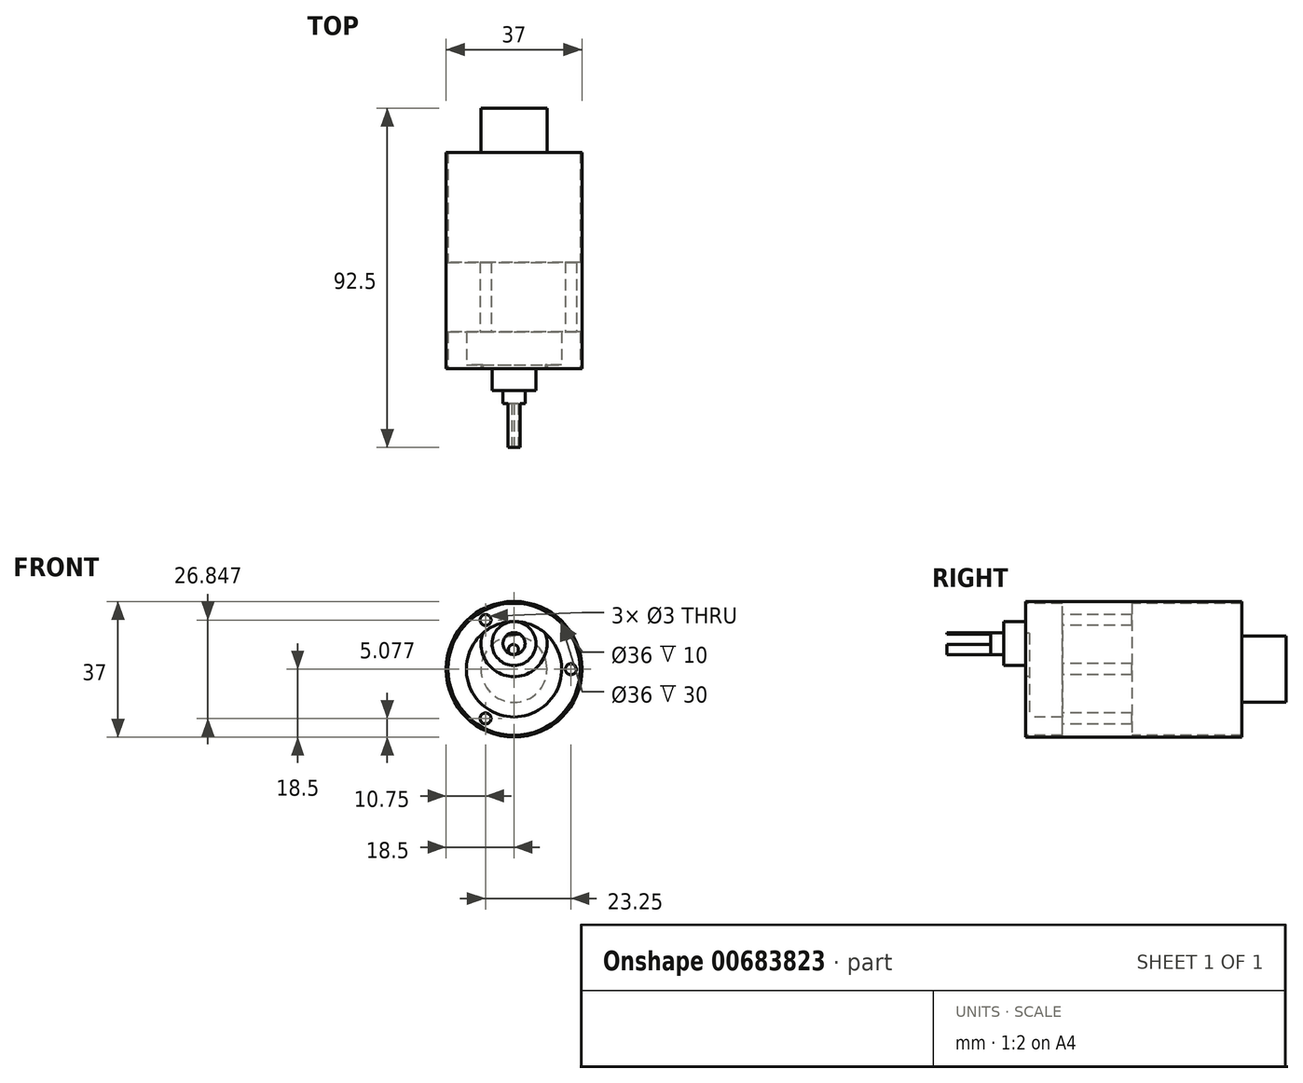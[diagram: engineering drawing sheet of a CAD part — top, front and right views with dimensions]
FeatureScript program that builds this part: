
annotation { "Feature Type Name" : "Feature", "Feature Type Description" : "" }
export const myFeature = defineFeature(function(context is Context, id is Id, definition is map)
    precondition{}
    {
        {
            var Q0;
            Q0=qCreatedBy(makeId("Front.planeOp"),FACE);
            var sketch = newSketch(context, id + "F0", { "sketchPlane" : qUnion([Q0])});
            skCircle(sketch, "E0", {"center": v(0, 0) * mm, "radius": 18.5 * mm});
            skCircle(sketch, "E1", {"center": v(0, 7) * mm, "radius": 6 * mm});
            skCircle(sketch, "E2", {"center": v(0, 0) * mm, "radius": 13 * mm});
            skCircle(sketch, "E3", {"center": v(-15.5, 0) * mm, "radius": 1.5 * mm});
            skCircle(sketch, "E4.MirrorC", {"center": v(15.5, 0) * mm, "radius": 1.5 * mm});
            skCircle(sketch, "E5.1.0", {"center": v(7.75, -13.42) * mm, "radius": 1.5 * mm});
            skCircle(sketch, "E5.1.1", {"center": v(-7.75, 13.42) * mm, "radius": 1.5 * mm});
            skCircle(sketch, "E5.2.0", {"center": v(7.75, 13.42) * mm, "radius": 1.5 * mm});
            skCircle(sketch, "E5.2.1", {"center": v(-7.75, -13.42) * mm, "radius": 1.5 * mm});
            skCircle(sketch, "E6", {"center": v(0, 7) * mm, "radius": 3 * mm});
            skCircle(sketch, "E7", {"center": v(0, 0) * mm, "radius": 18 * mm});
            skArc(sketch, "E8", {"start": v(-8.56, 9.79) * mm, "mid": v(0, -2) * mm, "end": v(8.56, 9.79) * mm});
            skSolve(sketch);
        }
        {
            var Q0;
            Q0=makeQuery(id+"F0.imprint","IMPRINT",FACE,{"disambiguationData":[TD([[makeQuery(id+"F0.imprint","IMPRINT",EDGE,{"derivedFrom":sQuery(id+"F0.wireOp",EDGE,"E0")}),1.0]])]});
            var Q1;
            Q1=makeQuery(id+"F0.imprint","IMPRINT",FACE,{"disambiguationData":[TD([[makeQuery(id+"F0.imprint","IMPRINT",EDGE,{"derivedFrom":sQuery(id+"F0.wireOp",EDGE,"E1")}),-1.0]])]});
            var Q2;
            Q2=makeQuery(id+"F0.imprint","IMPRINT",FACE,{"disambiguationData":[TD([[makeQuery(id+"F0.imprint","IMPRINT",EDGE,{"derivedFrom":sQuery(id+"F0.wireOp",EDGE,"E1")}),1.0]])]});
            var Q3;
            Q3=makeQuery(id+"F0.imprint","IMPRINT",FACE,{"disambiguationData":[TD([[makeQuery(id+"F0.imprint","IMPRINT",EDGE,{"derivedFrom":sQuery(id+"F0.wireOp",EDGE,"E3")}),1.0]])]});
            var Q4;
            Q4=makeQuery(id+"F0.imprint","IMPRINT",FACE,{"disambiguationData":[TD([[makeQuery(id+"F0.imprint","IMPRINT",EDGE,{"derivedFrom":sQuery(id+"F0.wireOp",EDGE,"E5.1.0")}),1.0]])]});
            var Q5;
            Q5=makeQuery(id+"F0.imprint","IMPRINT",FACE,{"disambiguationData":[TD([[makeQuery(id+"F0.imprint","IMPRINT",EDGE,{"derivedFrom":sQuery(id+"F0.wireOp",EDGE,"E4.MirrorC")}),-1.0]])]});
            var Q6;
            Q6=makeQuery(id+"F0.imprint","IMPRINT",FACE,{"disambiguationData":[TD([[makeQuery(id+"F0.imprint","IMPRINT",EDGE,{"derivedFrom":sQuery(id+"F0.wireOp",EDGE,"E5.2.0")}),1.0]])]});
            var Q7;
            Q7=makeQuery(id+"F0.imprint","IMPRINT",FACE,{"disambiguationData":[TD([[makeQuery(id+"F0.imprint","IMPRINT",EDGE,{"derivedFrom":sQuery(id+"F0.wireOp",EDGE,"E5.2.1")}),-1.0]])]});
            var Q8;
            Q8=makeQuery(id+"F0.imprint","IMPRINT",FACE,{"disambiguationData":[TD([[makeQuery(id+"F0.imprint","IMPRINT",EDGE,{"derivedFrom":sQuery(id+"F0.wireOp",EDGE,"E5.1.1")}),-1.0]])]});
            var Q9;
            Q9=makeQuery(id+"F0.imprint","IMPRINT",FACE,{"disambiguationData":[TD([[makeQuery(id+"F0.imprint","IMPRINT",EDGE,{"derivedFrom":sQuery(id+"F0.wireOp",EDGE,"E6")}),1.0]])]});
            var Q10;
            Q10=makeQuery(id+"F0.imprint","IMPRINT",FACE,{"disambiguationData":[TD([[makeQuery(id+"F0.imprint","IMPRINT",EDGE,{"derivedFrom":sQuery(id+"F0.wireOp",EDGE,"E2")}),-1.0]])]});
            var Q11;
            {var subQ0=sQuery(id+"F0.wireOp",EDGE,"E8");Q11=makeQuery(id+"F0.imprint","IMPRINT",FACE,{"disambiguationData":[TD([[makeQuery(id+"F0.imprint","IMPRINT",EDGE,{"derivedFrom":subQ0}),-1.0]])]});}
            extrude(context, id + "F1", {"entities" : qUnion([Q0, Q1, Q2, Q3, Q4, Q5, Q6, Q7, Q8, Q9, Q10, Q11]), "oppositeDirection" : true, "depth" : 29 * mm, "offsetDistance" : 25 * mm});
        }
        {
            var Q0;
            Q0=makeQuery(id+"F1.opExtrude","CAP_FACE",FACE,{"disambiguationData":[OSD([sQuery(id+"F0.wireOp",EDGE,"E0")])],"isStart":false});
            var sketch = newSketch(context, id + "F2", { "sketchPlane" : qUnion([Q0])});
            skCircle(sketch, "E9.0", {"center": v(0, 0) * mm, "radius": 18 * mm});
            skSolve(sketch);
        }
        {
            var Q0;
            Q0=makeQuery(id+"F2.imprint","IMPRINT",FACE,{"disambiguationData":[TD([[makeQuery(id+"F2.imprint","IMPRINT",EDGE,{"derivedFrom":sQuery(id+"F2.wireOp",EDGE,"E9.0")}),-1.0]])]});
            extrude(context, id + "F3", {"entities" : qUnion([Q0]), "operationType" : NewBodyOperationType.ADD, "depth" : 30 * mm, "offsetDistance" : 25 * mm});
        }
        {
            var Q0;
            Q0=makeQuery(id+"F3.opExtrude","CAP_FACE",FACE,{"disambiguationData":[OSD([sQuery(id+"F2.wireOp",EDGE,"E9.0")])],"isStart":false});
            var sketch = newSketch(context, id + "F4", { "sketchPlane" : qUnion([Q0])});
            skCircle(sketch, "E10", {"center": v(0, 0) * mm, "radius": 9 * mm});
            skSolve(sketch);
        }
        {
            var Q0;
            Q0=makeQuery(id+"F4.imprint","IMPRINT",FACE,{"disambiguationData":[TD([[makeQuery(id+"F4.imprint","IMPRINT",EDGE,{"derivedFrom":sQuery(id+"F4.wireOp",EDGE,"E10")}),1.0]])]});
            extrude(context, id + "F5", {"entities" : qUnion([Q0]), "operationType" : NewBodyOperationType.ADD, "depth" : 12 * mm, "offsetDistance" : 25 * mm});
        }
        {
            var Q0;
            Q0=makeQuery(id+"F0.imprint","IMPRINT",FACE,{"disambiguationData":[TD([[makeQuery(id+"F0.imprint","IMPRINT",EDGE,{"derivedFrom":sQuery(id+"F0.wireOp",EDGE,"E1")}),1.0]])]});
            extrude(context, id + "F6", {"entities" : qUnion([Q0]), "operationType" : NewBodyOperationType.ADD, "depth" : 6 * mm, "offsetDistance" : 25 * mm});
        }
        {
            var Q0;
            Q0=makeQuery(id+"F0.imprint","IMPRINT",FACE,{"disambiguationData":[TD([[makeQuery(id+"F0.imprint","IMPRINT",EDGE,{"derivedFrom":sQuery(id+"F0.wireOp",EDGE,"E6")}),1.0]])]});
            extrude(context, id + "F7", {"entities" : qUnion([Q0]), "operationType" : NewBodyOperationType.ADD, "depth" : (6 + 15.5) * mm, "offsetDistance" : 25 * mm});
        }
        {
            var Q0;
            Q0=makeQuery(id+"F0.imprint","IMPRINT",FACE,{"disambiguationData":[TD([[makeQuery(id+"F0.imprint","IMPRINT",EDGE,{"derivedFrom":sQuery(id+"F0.wireOp",EDGE,"E5.1.1")}),-1.0]])]});
            var Q1;
            Q1=makeQuery(id+"F0.imprint","IMPRINT",FACE,{"disambiguationData":[TD([[makeQuery(id+"F0.imprint","IMPRINT",EDGE,{"derivedFrom":sQuery(id+"F0.wireOp",EDGE,"E5.2.0")}),1.0]])]});
            var Q2;
            Q2=makeQuery(id+"F0.imprint","IMPRINT",FACE,{"disambiguationData":[TD([[makeQuery(id+"F0.imprint","IMPRINT",EDGE,{"derivedFrom":sQuery(id+"F0.wireOp",EDGE,"E4.MirrorC")}),-1.0]])]});
            var Q3;
            Q3=makeQuery(id+"F0.imprint","IMPRINT",FACE,{"disambiguationData":[TD([[makeQuery(id+"F0.imprint","IMPRINT",EDGE,{"derivedFrom":sQuery(id+"F0.wireOp",EDGE,"E5.2.1")}),-1.0]])]});
            var Q4;
            Q4=makeQuery(id+"F0.imprint","IMPRINT",FACE,{"disambiguationData":[TD([[makeQuery(id+"F0.imprint","IMPRINT",EDGE,{"derivedFrom":sQuery(id+"F0.wireOp",EDGE,"E3")}),1.0]])]});
            var Q5;
            Q5=makeQuery(id+"F0.imprint","IMPRINT",FACE,{"disambiguationData":[TD([[makeQuery(id+"F0.imprint","IMPRINT",EDGE,{"derivedFrom":sQuery(id+"F0.wireOp",EDGE,"E5.1.0")}),1.0]])]});
            extrude(context, id + "F8", {"entities" : qUnion([Q0, Q1, Q2, Q3, Q4, Q5]), "operationType" : NewBodyOperationType.REMOVE, "oppositeDirection" : true, "depth" : 10 * mm, "offsetDistance" : 25 * mm});
        }
        {
            var Q0;
            Q0=makeQuery(id+"F7.opExtrude","CAP_FACE",FACE,{"disambiguationData":[OSD([sQuery(id+"F0.wireOp",EDGE,"E6")])],"isStart":false});
            var sketch = newSketch(context, id + "F9", { "sketchPlane" : qUnion([Q0])});
            skCircle(sketch, "E11.0", {"center": v(0, 7) * mm, "radius": 3 * mm});
            skLineSegment(sketch, "E12.bottom", {"start": v(-7.35, 13.44) * mm, "end": v(6.01, 13.44) * mm});
            skLineSegment(sketch, "E12.top", {"start": v(-7.35, 9.5) * mm, "end": v(6.01, 9.5) * mm});
            skLineSegment(sketch, "E12.left", {"start": v(-7.35, 13.44) * mm, "end": v(-7.35, 9.5) * mm});
            skLineSegment(sketch, "E12.right", {"start": v(6.01, 13.44) * mm, "end": v(6.01, 9.5) * mm});
            skLineSegment(sketch, "E13", {"start": v(-3.45, 4) * mm, "end": v(3.7, 4) * mm});
            skCircle(sketch, "E14", {"center": v(-0.19, 5.36) * mm, "radius": 1.38 * mm});
            skPoint(sketch, "E14.first.point", {"position": v(0, 6.72) * mm});
            skPoint(sketch, "E14.second.point", {"position": v(0, 4) * mm});
            skPoint(sketch, "E14.third.point", {"position": v(-1.56, 5.28) * mm});
            skSolve(sketch);
        }
        {
            var Q0;
            Q0=makeQuery(id+"F9.imprint","IMPRINT",FACE,{"disambiguationData":[TD([[makeQuery(id+"F9.imprint","IMPRINT",EDGE,{"derivedFrom":sQuery(id+"F9.wireOp",EDGE,"E12.bottom")}),-1.0]])]});
            var Q1;
            {var subQ0=sQuery(id+"F9.wireOp",EDGE,"E12.top");var subQ1=sQuery(id+"F9.wireOp",EDGE,"E11.0");var subQ2=makeQuery(id+"F9.imprint","INTERSECT",VERTEX,{"disambiguationData":[OD(0.0)],"derivedFrom":[subQ1,subQ0]});Q1=makeQuery(id+"F9.imprint","IMPRINT",FACE,{"disambiguationData":[TD([[makeQuery(id+"F9.imprint","IMPRINT",EDGE,{"disambiguationData":[TD([[subQ2,1.0]])],"derivedFrom":subQ1}),1.0]])]});}
            extrude(context, id + "F10", {"entities" : qUnion([Q0, Q1]), "operationType" : NewBodyOperationType.REMOVE, "oppositeDirection" : true, "depth" : 12 * mm, "offsetDistance" : 25 * mm});
        }
        {
            var Q0;
            {var subQ0=sQuery(id+"F0.wireOp",EDGE,"E8");Q0=makeQuery(id+"F0.imprint","IMPRINT",FACE,{"disambiguationData":[TD([[makeQuery(id+"F0.imprint","IMPRINT",EDGE,{"derivedFrom":subQ0}),-1.0]])]});}
            extrude(context, id + "F11", {"entities" : qUnion([Q0]), "operationType" : NewBodyOperationType.REMOVE, "oppositeDirection" : true, "depth" : 1 * mm, "offsetDistance" : 25 * mm});
        }
    });
